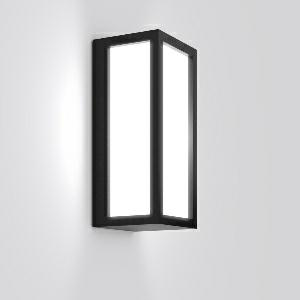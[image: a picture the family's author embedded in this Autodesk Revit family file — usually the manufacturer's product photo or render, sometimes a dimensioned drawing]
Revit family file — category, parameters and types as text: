
# Revit family: hb_101_611980_0031_cb7f
name_source: partatom
category: Lighting Fixtures
units: mm (PartAtom-declared; Revit-internal decimal feet)

## family parameters
Cut with Voids When Loaded = No
Host = Face
Light Source = No
Part Type = Normal
Room Calculation Point = No
Round Connector Dimension = Use Diameter
Shared = No

## types (1)
- HB 101 (1 x LED Modul 830, 810 lm, 3000)
    Apparent Load = 13 VA
    CIE Flux Codes = 12 37 67 50 100
    Color Rendering = 80
    Color Temperature = 3000
    Default Elevation = 1800 mm
    Description = Series: HB 101
Wall luminaire. Housing: die-cast aluminium, powder-coated. Diffuser: plastic (polycarbonate), opal. Driver integrated. 
Colour: anthracite metallic (DB703)
Length: 110 mm
Width: 103 mm
Height: 250 mm
Lamp: LED
System power: 13 W
Rated luminous flux: 810 lm
Luminous efficiency: 62 lm/W
Control gear: Regulated power supply
Protection class: I
Type of protection: IP 54
    Height = 250 mm
    Lamp = 1 x LED Modul 830
    Lamp Light Flux = 810 lm
    Lamp count = 1
    Length = 110 mm
    Lifetime = 50000 h
    Luminous efficacy = 62 lm/W
    Manufacturer = RZB
    ModVariant = No
    Model = 611980.0031
    Mounting Place = Wall
    Mounting Type = Surface mounted
    Number of Poles = 1
    OnlyDefault = Yes
    Power Factor = 1
    Product Name = HB 101
    Product group = Surface mounted Wall luminaires
    ProductGroupID = 2001
    Protection Class = Protection class I
    Protection Degree = IP 54
    RLX_Detail_Level = 1
    RLX_Emergency_Light_Flux = 0 lm
    RLX_Emergency_Type = 0
    RLX_Emergency_Type_DB = No
    RlxData = <blob elided: 57509 chars, md5=96c4bb7a>
    Socket = socket
    Standby Power = 0 W
    System Light Flux = 810 lm
    System Power = 13 W
    Type Comments = Product without accessories
    Type Image = 611980.0031.jpg
    URL = http://relux.com
    VarID = ---
    Voltage = 0 V
    Weight = 0.00 kg
    Width = 103 mm

## geometry (parser evidence)
native form markers: Blend x4, Sweep x14
no freeform markers — native parametric forms only
